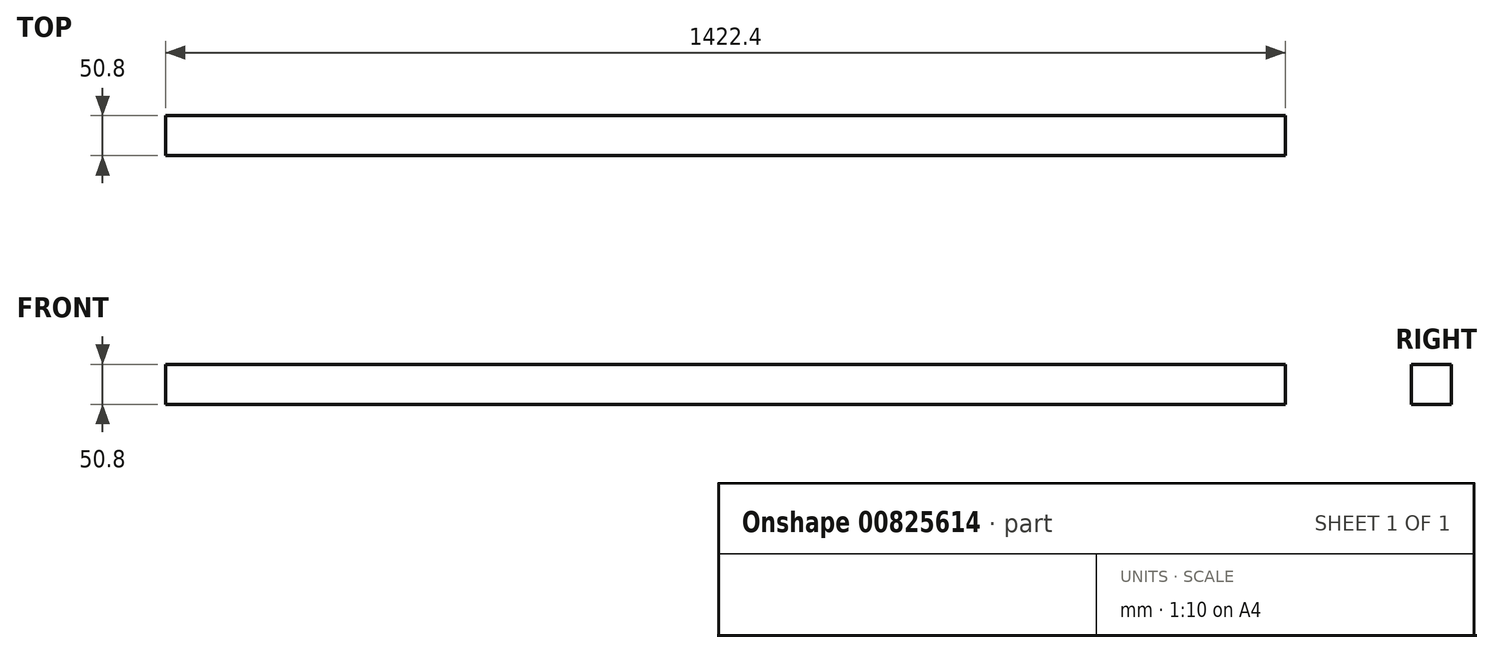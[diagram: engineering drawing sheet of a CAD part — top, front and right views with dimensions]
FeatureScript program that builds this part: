
annotation { "Feature Type Name" : "Feature", "Feature Type Description" : "" }
export const myFeature = defineFeature(function(context is Context, id is Id, definition is map)
    precondition{}
    {
        {
            var Q0;
            Q0=qCreatedBy(makeId("Right.planeOp"),FACE);
            var sketch = newSketch(context, id + "F0", { "sketchPlane" : qUnion([Q0])});
            skLineSegment(sketch, "E0.bottom", {"start": v(-20.27, -18.52) * mm, "end": v(30.53, -18.52) * mm});
            skLineSegment(sketch, "E0.top", {"start": v(-20.27, 32.28) * mm, "end": v(30.53, 32.28) * mm});
            skLineSegment(sketch, "E0.left", {"start": v(-20.27, -18.52) * mm, "end": v(-20.27, 32.28) * mm});
            skLineSegment(sketch, "E0.right", {"start": v(30.53, -18.52) * mm, "end": v(30.53, 32.28) * mm});
            skSolve(sketch);
        }
        {
            var Q0;
            Q0 = qSketchRegion(id + "F0", true);
            extrude(context, id + "F1", {"entities" : qUnion([Q0]), "depth" : 1422.4 * mm, "offsetDistance" : 25.4 * mm});
        }
    });
